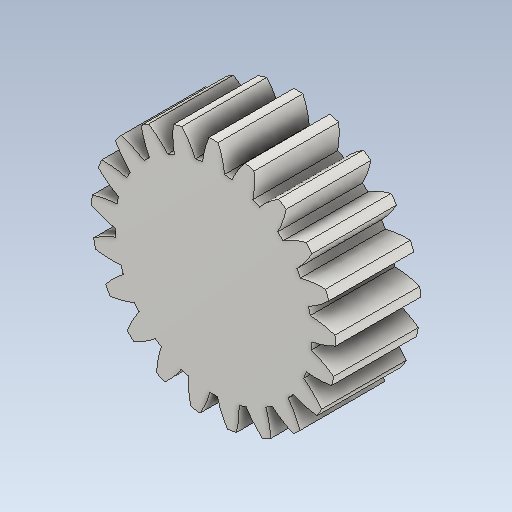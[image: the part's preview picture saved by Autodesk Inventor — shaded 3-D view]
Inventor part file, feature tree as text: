
AUTODESK INVENTOR PART (.ipt)
format: ipt  version: 2020 (Build 240168000, 168)  size: 258,560 bytes
history: native  units: mm (DEFAULTED — no unit token found)
features: plane x3, other x3, sketch x2, extrude x1
ambient origin geometry x8: Origin, YZ Plane, XZ Plane, XY Plane, X Axis, Y Axis, Z Axis, Center Point
bodies: Solid1 (feature_tree)
feature tree (9):
  extrude  "Extrusion1"  Depth=7.6mm TaperAngle=0.0deg
  plane  "Work Plane2"
  plane  "Work Plane8"
  plane  "Work Plane9"
  other  "Przekładnia walcowa"
  sketch  "Sketch1"  dims[d0=21.899062mm d1=7.6mm d2=0.0mm]
  sketch  "Sketch2"  dims[d3=20.0mm d4=10.0mm d5=0.0mm d16=30.0mm d17=0.0mm d34=1.495997mm d39=0.0mm d41=0.0mm d43=30.0mm d46=30.0mm d47=0.0mm d48=0.0mm]
  other  "Srf1"
  other  "Średnica podziałowa"
